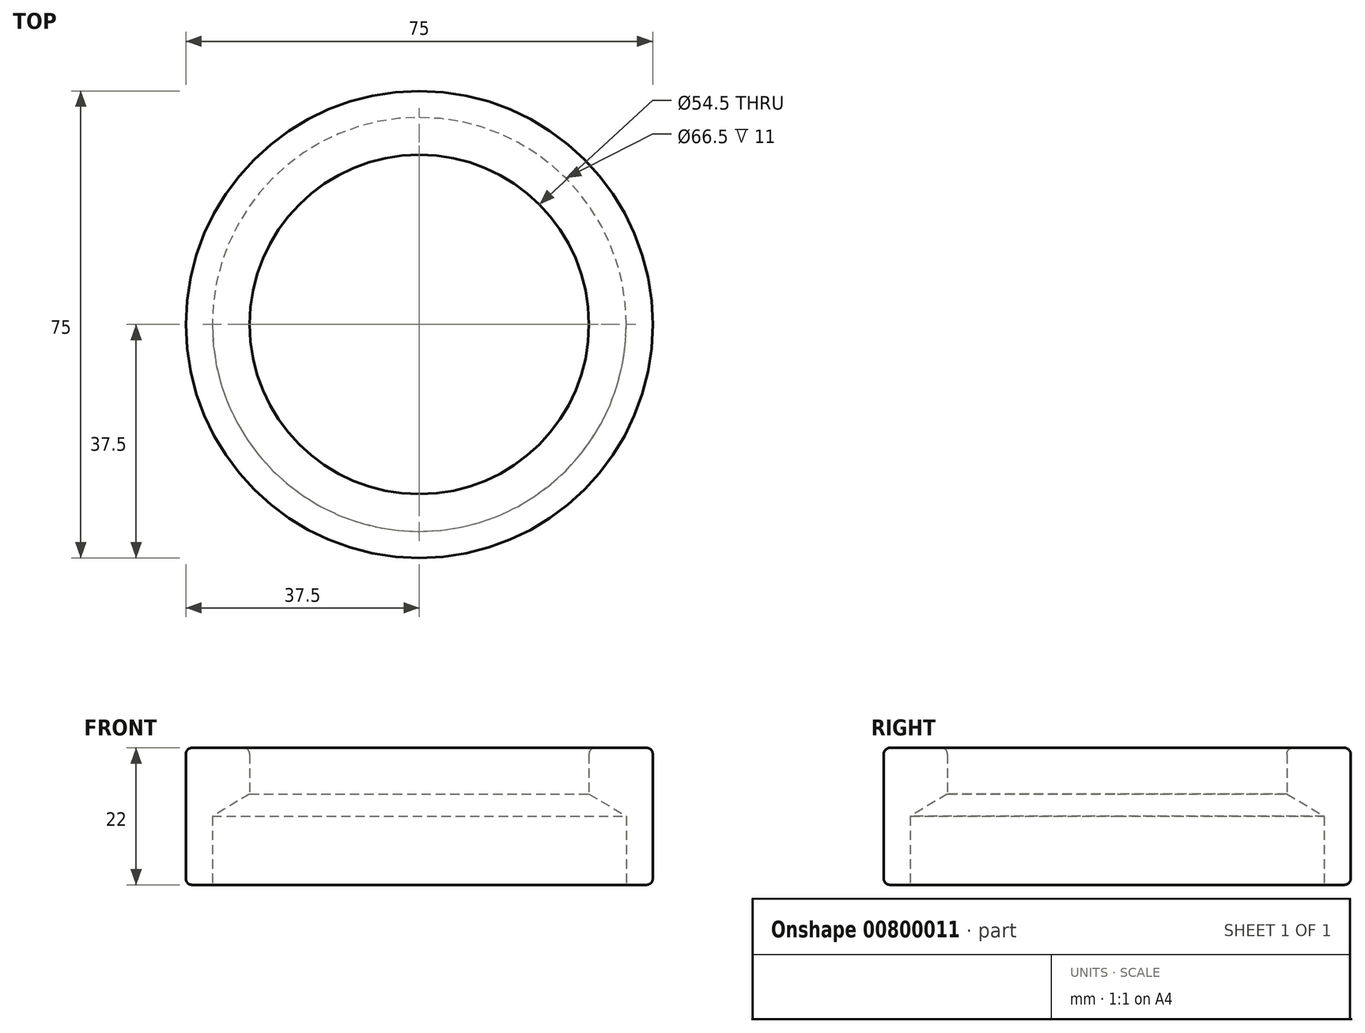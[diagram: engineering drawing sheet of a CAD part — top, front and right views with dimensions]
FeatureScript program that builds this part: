
annotation { "Feature Type Name" : "Feature", "Feature Type Description" : "" }
export const myFeature = defineFeature(function(context is Context, id is Id, definition is map)
    precondition{}
    {
        {
            assignVariable(context, id + "F0", {"name" : "Base_OD", "anyValue" : 66.5 * mm});
        }
        {
            assignVariable(context, id + "F1", {"name" : "Brim_height", "anyValue" : 22 * mm});
        }
        {
            var Q0;
            Q0=qCreatedBy(makeId("Top.planeOp"),FACE);
            var sketch = newSketch(context, id + "F2", { "sketchPlane" : qUnion([Q0])});
            skCircle(sketch, "E0", {"center": v(0, 0) * mm, "radius": 37.5 * mm});
            skCircle(sketch, "E1", {"center": v(0, 0) * mm, "radius": 27.25 * mm});
            skCircle(sketch, "E2", {"center": v(0, 0) * mm, "radius": 33.25 * mm});
            skSolve(sketch);
        }
        {
            var Q0;
            Q0=makeQuery(id+"F2.imprint","IMPRINT",FACE,{"disambiguationData":[TD([[makeQuery(id+"F2.imprint","IMPRINT",EDGE,{"derivedFrom":sQuery(id+"F2.wireOp",EDGE,"E0")}),1.0]])]});
            var Q1;
            Q1=makeQuery(id+"F2.imprint","IMPRINT",FACE,{"disambiguationData":[TD([[makeQuery(id+"F2.imprint","IMPRINT",EDGE,{"derivedFrom":sQuery(id+"F2.wireOp",EDGE,"E1")}),-1.0]])]});
            extrude(context, id + "F3", {"entities" : qUnion([Q0, Q1]), "depth" : getVariable(context, 'Brim_height'), "offsetDistance" : 25 * mm});
        }
        {
            var Q0;
            Q0=makeQuery(id+"F2.imprint","IMPRINT",FACE,{"disambiguationData":[TD([[makeQuery(id+"F2.imprint","IMPRINT",EDGE,{"derivedFrom":sQuery(id+"F2.wireOp",EDGE,"E1")}),-1.0]])]});
            extrude(context, id + "F4", {"entities" : qUnion([Q0]), "operationType" : NewBodyOperationType.REMOVE, "depth" : getVariable(context, 'Brim_height') / 2, "offsetDistance" : 25 * mm});
        }
        {
            var Q0;
            Q0=makeQuery(id+"F3.opExtrude","CAP_EDGE",EDGE,{"disambiguationData":[OSD([sQuery(id+"F2.wireOp",EDGE,"E0")])],"isStart":false});
            var Q1;
            Q1=makeQuery(id+"F3.opExtrude","CAP_EDGE",EDGE,{"disambiguationData":[OSD([sQuery(id+"F2.wireOp",EDGE,"E1")])],"isStart":false});
            var Q2;
            Q2=makeQuery(id+"F3.opExtrude","CAP_EDGE",EDGE,{"disambiguationData":[OSD([sQuery(id+"F2.wireOp",EDGE,"E0")])],"isStart":true});
            fillet(context, id + "F5", {"entities" : qUnion([Q0, Q1, Q2]), "radius" : 1 * mm, "tangentPropagation" : true, "allowEdgeOverflow" : false});
        }
        {
            var Q0;
            Q0=sQuery(id+"F2.wireOp",VERTEX,"E0.center");
            var Q1;
            Q1=makeQuery(id+"F3.opExtrude","SWEPT_BODY",BODY,{"disambiguationData":[OSD([sQuery(id+"F2.wireOp",EDGE,"E0"),sQuery(id+"F2.wireOp",EDGE,"E1")])]});
            hole(context, id + "F6", {"style" : HoleStyle.SIMPLE, "endStyle" : HoleEndStyle.BLIND, "oppositeDirection" : true, "holeDiameter" : getVariable(context, 'Base_OD'), "majorDiameter" : 5 * mm, "holeDepth" : getVariable(context, 'Brim_height') / 2, "isTappedThrough" : true, "tappedDepth" : 12 * mm, "tapClearance" : 3, "locations" : qUnion([Q0]), "scope" : qUnion([Q1])});
        }
    });
